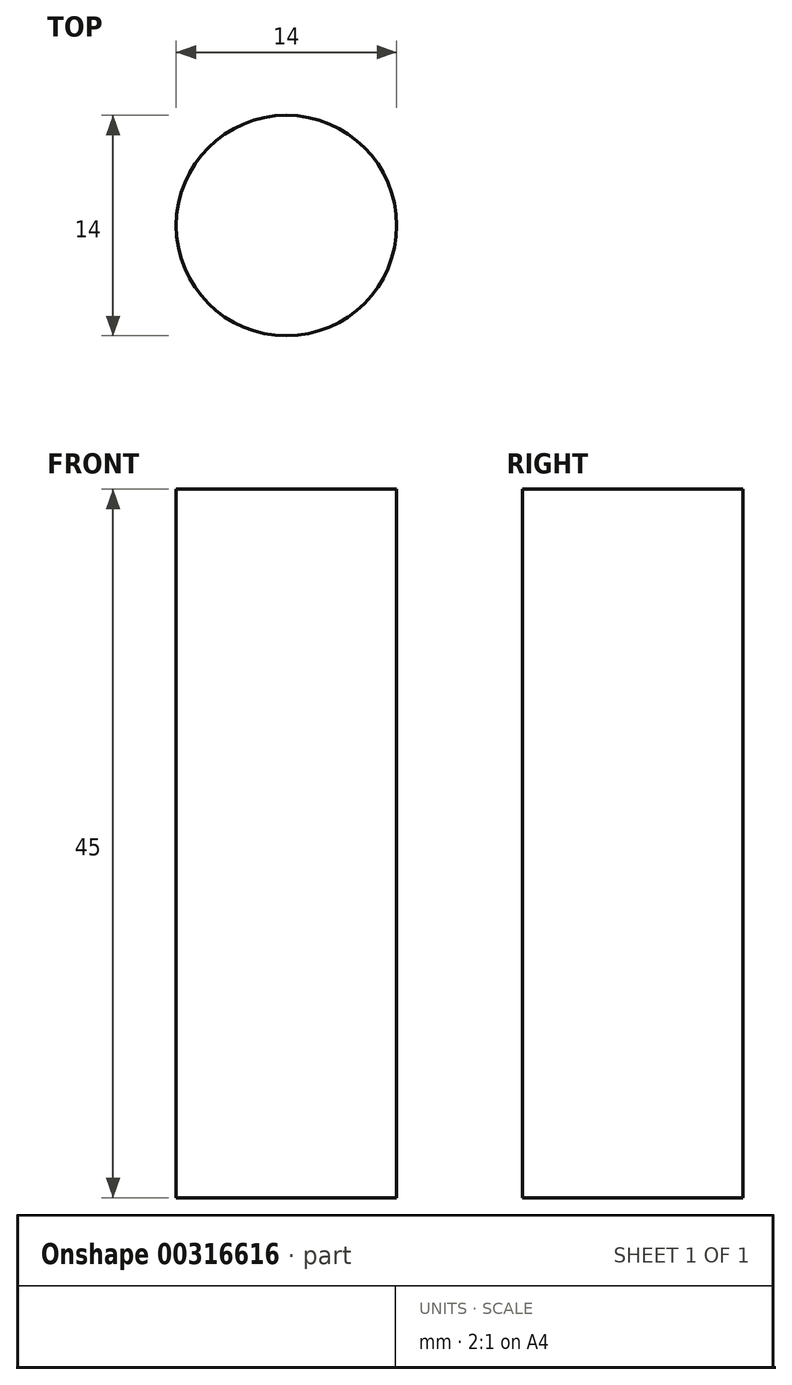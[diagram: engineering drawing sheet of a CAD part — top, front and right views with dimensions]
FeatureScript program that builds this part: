
annotation { "Feature Type Name" : "Feature", "Feature Type Description" : "" }
export const myFeature = defineFeature(function(context is Context, id is Id, definition is map)
    precondition{}
    {
        {
            var Q0;
            Q0=qCreatedBy(makeId("Top.planeOp"),FACE);
            var sketch = newSketch(context, id + "F0", { "sketchPlane" : qUnion([Q0])});
            skCircle(sketch, "E0", {"center": v(0, 0) * mm, "radius": 7 * mm});
            skSolve(sketch);
        }
        {
            var Q0;
            Q0=makeQuery(id+"F0.imprint","IMPRINT",FACE,{"disambiguationData":[TD([[makeQuery(id+"F0.imprint","IMPRINT",EDGE,{"derivedFrom":sQuery(id+"F0.wireOp",EDGE,"E0")}),1.0]])]});
            extrude(context, id + "F1", {"entities" : qUnion([Q0]), "depth" : 45 * mm});
        }
    });
